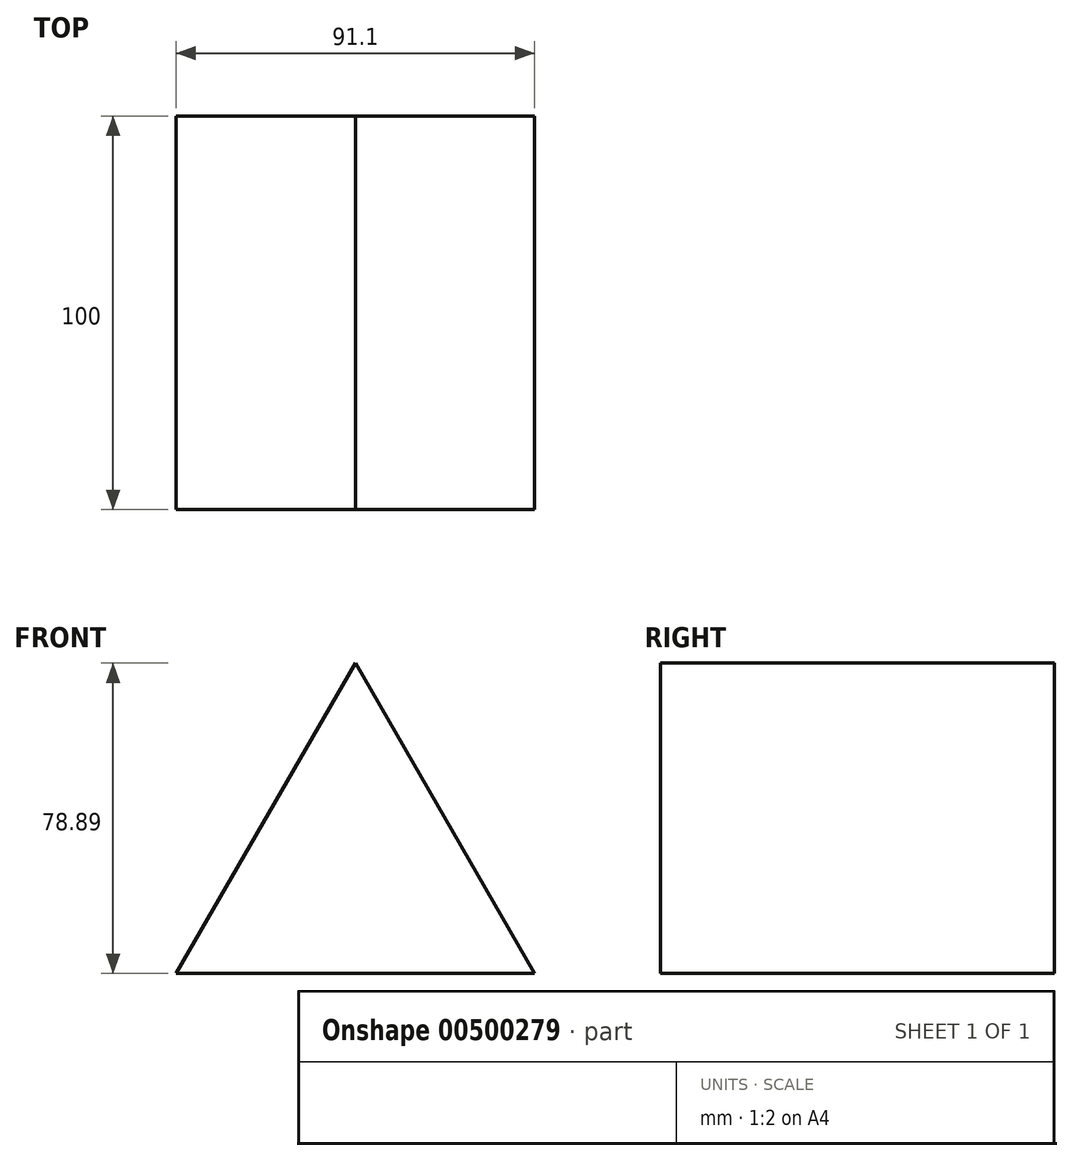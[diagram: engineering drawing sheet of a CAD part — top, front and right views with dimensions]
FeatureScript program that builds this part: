
annotation { "Feature Type Name" : "Feature", "Feature Type Description" : "" }
export const myFeature = defineFeature(function(context is Context, id is Id, definition is map)
    precondition{}
    {
        {
            var Q0;
            Q0=qCreatedBy(makeId("Front.planeOp"),FACE);
            var sketch = newSketch(context, id + "F0", { "sketchPlane" : qUnion([Q0])});
            skCircle(sketch, "E0.cCircle", {"center": v(0, 0) * mm, "radius": 52.6 * mm, "construction": true});
            skLineSegment(sketch, "E0.0", {"start": v(-45.55, -26.3) * mm, "end": v(0, 52.6) * mm});
            skLineSegment(sketch, "E0.1", {"start": v(0, 52.6) * mm, "end": v(45.55, -26.3) * mm});
            skLineSegment(sketch, "E0.2", {"start": v(45.55, -26.3) * mm, "end": v(-45.55, -26.3) * mm});
            skSolve(sketch);
        }
        {
            var Q0;
            Q0=makeQuery(id+"F0.imprint","IMPRINT",FACE,{"disambiguationData":[TD([[makeQuery(id+"F0.imprint","IMPRINT",EDGE,{"derivedFrom":sQuery(id+"F0.wireOp",EDGE,"E0.0")}),-1.0]])]});
            extrude(context, id + "F1", {"entities" : qUnion([Q0]), "depth" : 100 * mm});
        }
    });
